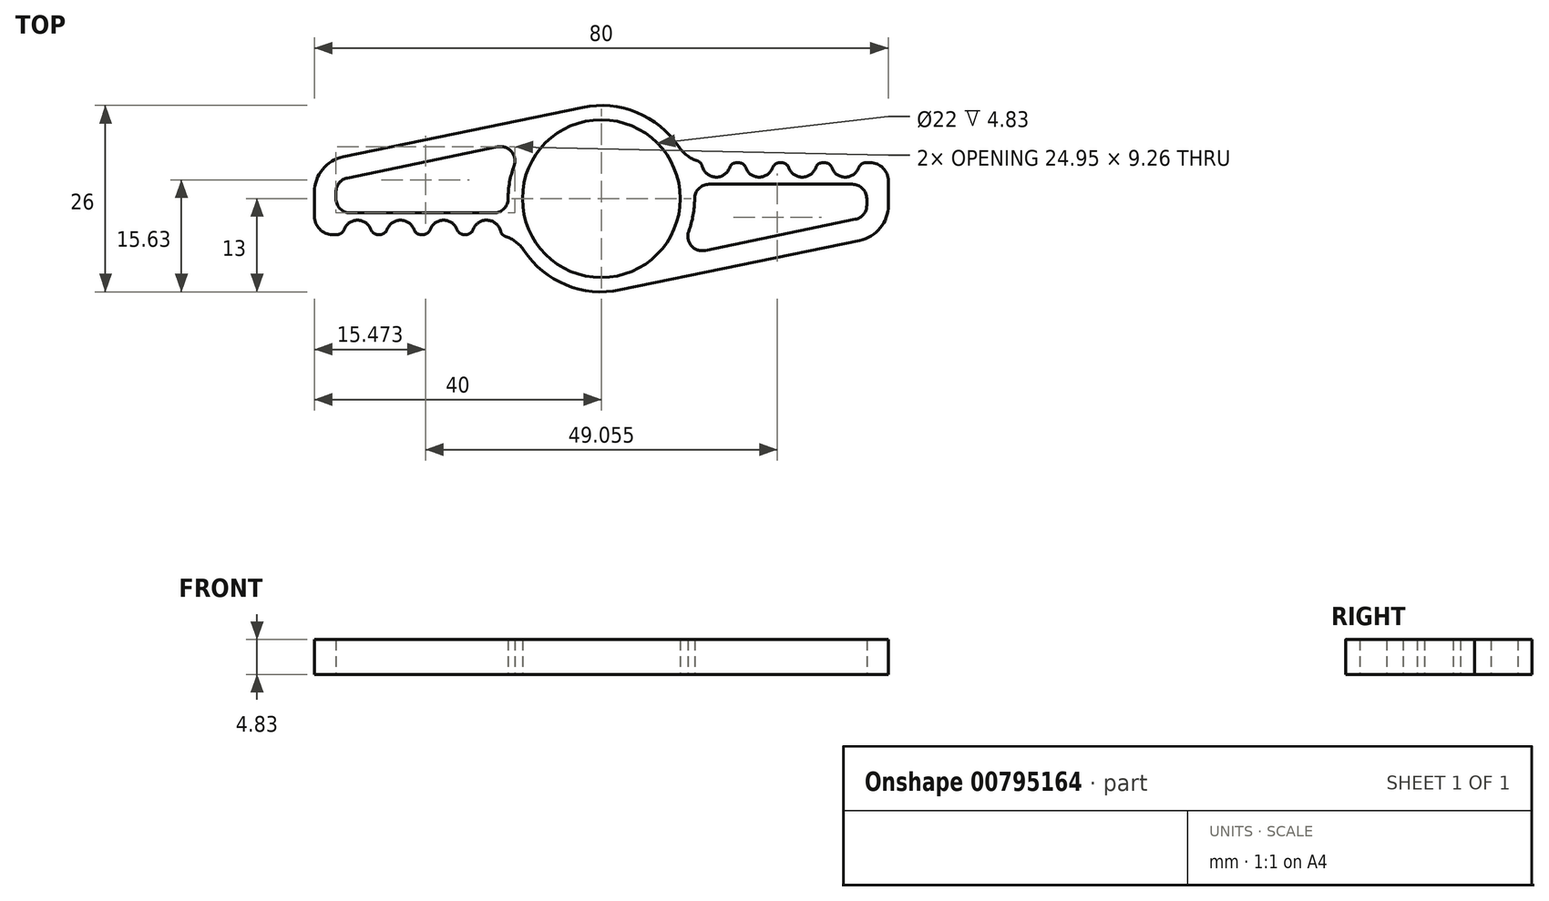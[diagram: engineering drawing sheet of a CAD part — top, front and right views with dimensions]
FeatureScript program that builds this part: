
annotation { "Feature Type Name" : "Feature", "Feature Type Description" : "" }
export const myFeature = defineFeature(function(context is Context, id is Id, definition is map)
    precondition{}
    {
        {
            var Q0;
            Q0=qCreatedBy(makeId("Top.planeOp"),FACE);
            var sketch = newSketch(context, id + "F0", { "sketchPlane" : qUnion([Q0])});
            skCircle(sketch, "E0", {"center": v(0, 0) * mm, "radius": 11 * mm});
            skArc(sketch, "E1", {"start": v(-12.17, 4.56) * mm, "mid": v(-12.8, 2.32) * mm, "end": v(-13, 0) * mm});
            skLineSegment(sketch, "E2", {"start": v(-40, 0.93) * mm, "end": v(-40, -2.5) * mm});
            skLineSegment(sketch, "E3", {"start": v(-36.01, 5.82) * mm, "end": v(-2.63, 12.73) * mm});
            skLineSegment(sketch, "E4", {"start": v(-37.5, -5) * mm, "end": v(-36.83, -5) * mm});
            skPoint(sketch, "E5.visualSharp", {"position": v(-40, 5) * mm});
            skArc(sketch, "E5.filletArc", {"start": v(-36.01, 5.82) * mm, "mid": v(-38.88, 4.09) * mm, "end": v(-40, 0.93) * mm});
            skPoint(sketch, "E6.visualSharp", {"position": v(-40, -5) * mm});
            skArc(sketch, "E6.filletArc", {"start": v(-40, -2.5) * mm, "mid": v(-39.27, -4.27) * mm, "end": v(-37.5, -5) * mm});
            skPoint(sketch, "E7.visualSharp", {"position": v(-12, -5) * mm});
            skArc(sketch, "E7.filletArc", {"start": v(-10.8, -7.22) * mm, "mid": v(-11.94, -6.02) * mm, "end": v(-13.4, -5.25) * mm});
            skArc(sketch, "E8", {"start": v(-32.11, -4.33) * mm, "mid": v(-34, -3) * mm, "end": v(-35.89, -4.33) * mm});
            skArc(sketch, "E9.1.0.0", {"start": v(-26.11, -4.33) * mm, "mid": v(-28, -3) * mm, "end": v(-29.89, -4.33) * mm});
            skArc(sketch, "E9.2.0.0", {"start": v(-20.11, -4.33) * mm, "mid": v(-22, -3) * mm, "end": v(-23.89, -4.33) * mm});
            skArc(sketch, "E9.3.0.0", {"start": v(-14.05, -4.54) * mm, "mid": v(-15.9, -3) * mm, "end": v(-17.89, -4.33) * mm});
            skLineSegment(sketch, "E10.3", {"start": v(-35.4, 2.89) * mm, "end": v(-14.45, 7.22) * mm});
            skLineSegment(sketch, "E10.4", {"start": v(-35, -2) * mm, "end": v(-15, -2) * mm});
            skLineSegment(sketch, "E10.5", {"start": v(-37, 0.93) * mm, "end": v(-37, 0) * mm});
            skArc(sketch, "E11.trimOffspring", {"start": v(-10.8, -7.22) * mm, "mid": v(-4.93, -12.03) * mm, "end": v(2.63, -12.73) * mm});
            skPoint(sketch, "E12.visualSharp", {"position": v(-37, 2.56) * mm});
            skArc(sketch, "E12.filletArc", {"start": v(-35.4, 2.89) * mm, "mid": v(-36.55, 2.2) * mm, "end": v(-37, 0.93) * mm});
            skPoint(sketch, "E13.visualSharp", {"position": v(-37, -2) * mm});
            skArc(sketch, "E13.filletArc", {"start": v(-37, 0) * mm, "mid": v(-36.41, -1.41) * mm, "end": v(-35, -2) * mm});
            skArc(sketch, "E14.filletArc", {"start": v(-15, -2) * mm, "mid": v(-13.59, -1.41) * mm, "end": v(-13, 0) * mm});
            skPoint(sketch, "E15.visualSharp", {"position": v(-10.16, 8.1) * mm});
            skArc(sketch, "E15.filletArc", {"start": v(-12.17, 4.56) * mm, "mid": v(-12.53, 6.56) * mm, "end": v(-14.45, 7.22) * mm});
            skLineSegment(sketch, "E16.trimOffspring", {"start": v(-25.17, -5) * mm, "end": v(-24.83, -5) * mm});
            skLineSegment(sketch, "E17.trimOffspring", {"start": v(-19.17, -5) * mm, "end": v(-18.83, -5) * mm});
            skPoint(sketch, "E18.visualSharp", {"position": v(-36, -5) * mm});
            skArc(sketch, "E18.filletArc", {"start": v(-36.83, -5) * mm, "mid": v(-36.25, -4.82) * mm, "end": v(-35.89, -4.33) * mm});
            skPoint(sketch, "E19.visualSharp", {"position": v(-32, -5) * mm});
            skArc(sketch, "E19.filletArc", {"start": v(-32.11, -4.33) * mm, "mid": v(-31.75, -4.82) * mm, "end": v(-31.17, -5) * mm});
            skPoint(sketch, "E20.visualSharp", {"position": v(-30, -5) * mm});
            skArc(sketch, "E20.filletArc", {"start": v(-30.83, -5) * mm, "mid": v(-30.25, -4.82) * mm, "end": v(-29.89, -4.33) * mm});
            skPoint(sketch, "E21.visualSharp", {"position": v(-26, -5) * mm});
            skArc(sketch, "E21.filletArc", {"start": v(-26.11, -4.33) * mm, "mid": v(-25.75, -4.82) * mm, "end": v(-25.17, -5) * mm});
            skPoint(sketch, "E22.visualSharp", {"position": v(-24, -5) * mm});
            skArc(sketch, "E22.filletArc", {"start": v(-24.83, -5) * mm, "mid": v(-24.25, -4.82) * mm, "end": v(-23.89, -4.33) * mm});
            skPoint(sketch, "E23.visualSharp", {"position": v(-20, -5) * mm});
            skArc(sketch, "E23.filletArc", {"start": v(-20.11, -4.33) * mm, "mid": v(-19.75, -4.82) * mm, "end": v(-19.17, -5) * mm});
            skPoint(sketch, "E24.visualSharp", {"position": v(-18, -5) * mm});
            skArc(sketch, "E24.filletArc", {"start": v(-18.83, -5) * mm, "mid": v(-18.25, -4.82) * mm, "end": v(-17.89, -4.33) * mm});
            skPoint(sketch, "E25.visualSharp", {"position": v(-14, -5.1) * mm});
            skArc(sketch, "E25.filletArc", {"start": v(-14.05, -4.54) * mm, "mid": v(-13.82, -4.98) * mm, "end": v(-13.4, -5.25) * mm});
            skLineSegment(sketch, "E26", {"start": v(-31.17, -5) * mm, "end": v(-30.83, -5) * mm});
            skPoint(sketch, "E27.1.0", {"position": v(18, 5) * mm});
            skArc(sketch, "E27.1.1", {"start": v(36.01, -5.82) * mm, "mid": v(38.88, -4.09) * mm, "end": v(40, -0.93) * mm});
            skPoint(sketch, "E27.1.2", {"position": v(40, 5) * mm});
            skPoint(sketch, "E27.1.3", {"position": v(30, 5) * mm});
            skArc(sketch, "E27.1.4", {"start": v(26.11, 4.33) * mm, "mid": v(28, 3) * mm, "end": v(29.89, 4.33) * mm});
            skArc(sketch, "E27.1.5", {"start": v(12.17, -4.56) * mm, "mid": v(12.8, -2.32) * mm, "end": v(13, 0) * mm});
            skPoint(sketch, "E27.1.6", {"position": v(10.16, -8.1) * mm});
            skArc(sketch, "E27.1.7", {"start": v(32.11, 4.33) * mm, "mid": v(34, 3) * mm, "end": v(35.89, 4.33) * mm});
            skLineSegment(sketch, "E27.1.8", {"start": v(40, -0.93) * mm, "end": v(40, 2.5) * mm});
            skPoint(sketch, "E27.1.9", {"position": v(14, 5.1) * mm});
            skArc(sketch, "E27.1.10", {"start": v(40, 2.5) * mm, "mid": v(39.27, 4.27) * mm, "end": v(37.5, 5) * mm});
            skArc(sketch, "E27.1.11", {"start": v(20.11, 4.33) * mm, "mid": v(22, 3) * mm, "end": v(23.89, 4.33) * mm});
            skPoint(sketch, "E27.1.12", {"position": v(37, 2) * mm});
            skArc(sketch, "E27.1.13", {"start": v(37, 0) * mm, "mid": v(36.41, 1.41) * mm, "end": v(35, 2) * mm});
            skPoint(sketch, "E27.1.14", {"position": v(40, -5) * mm});
            skArc(sketch, "E27.1.15", {"start": v(10.8, 7.22) * mm, "mid": v(11.94, 6.02) * mm, "end": v(13.4, 5.25) * mm});
            skLineSegment(sketch, "E27.1.16", {"start": v(35.4, -2.89) * mm, "end": v(14.45, -7.22) * mm});
            skArc(sketch, "E27.1.17", {"start": v(14.05, 4.54) * mm, "mid": v(15.9, 3) * mm, "end": v(17.89, 4.33) * mm});
            skPoint(sketch, "E27.1.18", {"position": v(36, 5) * mm});
            skPoint(sketch, "E27.1.19", {"position": v(24, 5) * mm});
            skPoint(sketch, "E27.1.20", {"position": v(26, 5) * mm});
            skPoint(sketch, "E27.1.21", {"position": v(12, 5) * mm});
            skLineSegment(sketch, "E27.1.22", {"start": v(35, 2) * mm, "end": v(15, 2) * mm});
            skPoint(sketch, "E27.1.23", {"position": v(20, 5) * mm});
            skArc(sketch, "E27.1.24", {"start": v(12.17, -4.56) * mm, "mid": v(12.53, -6.56) * mm, "end": v(14.45, -7.22) * mm});
            skPoint(sketch, "E27.1.25", {"position": v(32, 5) * mm});
            skArc(sketch, "E27.1.26", {"start": v(15, 2) * mm, "mid": v(13.59, 1.41) * mm, "end": v(13, 0) * mm});
            skPoint(sketch, "E27.1.27", {"position": v(37, -2.56) * mm});
            skArc(sketch, "E27.1.28", {"start": v(35.4, -2.89) * mm, "mid": v(36.55, -2.2) * mm, "end": v(37, -0.93) * mm});
            skArc(sketch, "E27.1.29", {"start": v(24.83, 5) * mm, "mid": v(24.25, 4.82) * mm, "end": v(23.89, 4.33) * mm});
            skLineSegment(sketch, "E27.1.30", {"start": v(37.5, 5) * mm, "end": v(36.83, 5) * mm});
            skArc(sketch, "E27.1.31", {"start": v(18.83, 5) * mm, "mid": v(18.25, 4.82) * mm, "end": v(17.89, 4.33) * mm});
            skArc(sketch, "E27.1.32", {"start": v(30.83, 5) * mm, "mid": v(30.25, 4.82) * mm, "end": v(29.89, 4.33) * mm});
            skArc(sketch, "E27.1.33", {"start": v(14.05, 4.54) * mm, "mid": v(13.82, 4.98) * mm, "end": v(13.4, 5.25) * mm});
            skArc(sketch, "E27.1.34", {"start": v(20.11, 4.33) * mm, "mid": v(19.75, 4.82) * mm, "end": v(19.17, 5) * mm});
            skArc(sketch, "E27.1.35", {"start": v(32.11, 4.33) * mm, "mid": v(31.75, 4.82) * mm, "end": v(31.17, 5) * mm});
            skLineSegment(sketch, "E27.1.36", {"start": v(37, -0.93) * mm, "end": v(37, 0) * mm});
            skArc(sketch, "E27.1.37", {"start": v(26.11, 4.33) * mm, "mid": v(25.75, 4.82) * mm, "end": v(25.17, 5) * mm});
            skArc(sketch, "E27.1.38", {"start": v(36.83, 5) * mm, "mid": v(36.25, 4.82) * mm, "end": v(35.89, 4.33) * mm});
            skLineSegment(sketch, "E27.1.39", {"start": v(31.17, 5) * mm, "end": v(30.83, 5) * mm});
            skLineSegment(sketch, "E27.1.40", {"start": v(19.17, 5) * mm, "end": v(18.83, 5) * mm});
            skLineSegment(sketch, "E27.1.41", {"start": v(25.17, 5) * mm, "end": v(24.83, 5) * mm});
            skLineSegment(sketch, "E27.1.42", {"start": v(36.01, -5.82) * mm, "end": v(2.63, -12.73) * mm});
            skArc(sketch, "E28.trimOffspring", {"start": v(10.8, 7.22) * mm, "mid": v(4.93, 12.03) * mm, "end": v(-2.63, 12.73) * mm});
            skSolve(sketch);
        }
        {
            var Q0;
            Q0=makeQuery(id+"F0.imprint","IMPRINT",FACE,{"disambiguationData":[TD([[makeQuery(id+"F0.imprint","IMPRINT",EDGE,{"derivedFrom":sQuery(id+"F0.wireOp",EDGE,"E0")}),-1.0]])]});
            extrude(context, id + "F1", {"entities" : qUnion([Q0]), "depth" : 4.83 * mm, "offsetDistance" : 25 * mm});
        }
    });
